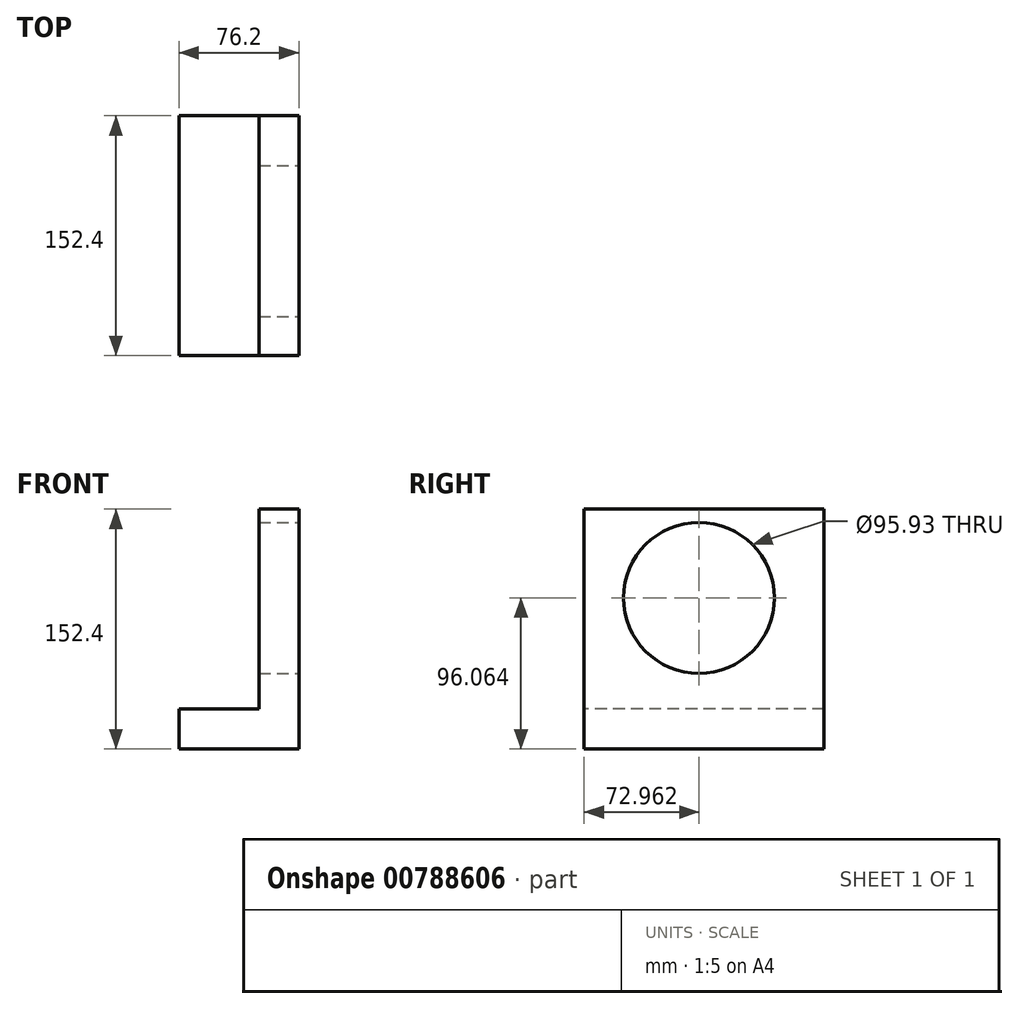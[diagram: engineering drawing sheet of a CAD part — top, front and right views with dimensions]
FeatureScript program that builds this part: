
annotation { "Feature Type Name" : "Feature", "Feature Type Description" : "" }
export const myFeature = defineFeature(function(context is Context, id is Id, definition is map)
    precondition{}
    {
        {
            var Q0;
            Q0=qCreatedBy(makeId("Front.planeOp"),FACE);
            var sketch = newSketch(context, id + "F0", { "sketchPlane" : qUnion([Q0])});
            skLineSegment(sketch, "E0", {"start": v(0, 0) * mm, "end": v(0, 152.4) * mm});
            skLineSegment(sketch, "E1", {"start": v(0, 152.4) * mm, "end": v(-25.4, 152.4) * mm});
            skLineSegment(sketch, "E2", {"start": v(-25.4, 152.4) * mm, "end": v(-25.4, 25.4) * mm});
            skLineSegment(sketch, "E3", {"start": v(-25.4, 25.4) * mm, "end": v(-76.2, 25.4) * mm});
            skLineSegment(sketch, "E4", {"start": v(-76.2, 25.4) * mm, "end": v(-76.2, 0) * mm});
            skLineSegment(sketch, "E5", {"start": v(-76.2, 0) * mm, "end": v(0, 0) * mm});
            skSolve(sketch);
        }
        {
            var Q0;
            Q0 = qSketchRegion(id + "F0", true);
            var Q1;
            Q1 = qSketchRegion(id + "F2", true);
            extrude(context, id + "F1", {"entities" : qUnion([Q0, Q1]), "oppositeDirection" : true, "depth" : 152.4 * mm, "offsetDistance" : 25.4 * mm});
        }
        {
            var Q0;
            Q0=qCreatedBy(makeId("Right.planeOp"),FACE);
            var sketch = newSketch(context, id + "F2", { "sketchPlane" : qUnion([Q0])});
            skCircle(sketch, "E6", {"center": v(72.96, 96.06) * mm, "radius": 47.96 * mm});
            skSolve(sketch);
        }
        {
            var Q0;
            Q0 = qSketchRegion(id + "F2", true);
            extrude(context, id + "F3", {"entities" : qUnion([Q0]), "operationType" : NewBodyOperationType.REMOVE, "oppositeDirection" : true, "depth" : 152.4 * mm, "offsetDistance" : 25.4 * mm});
        }
    });
